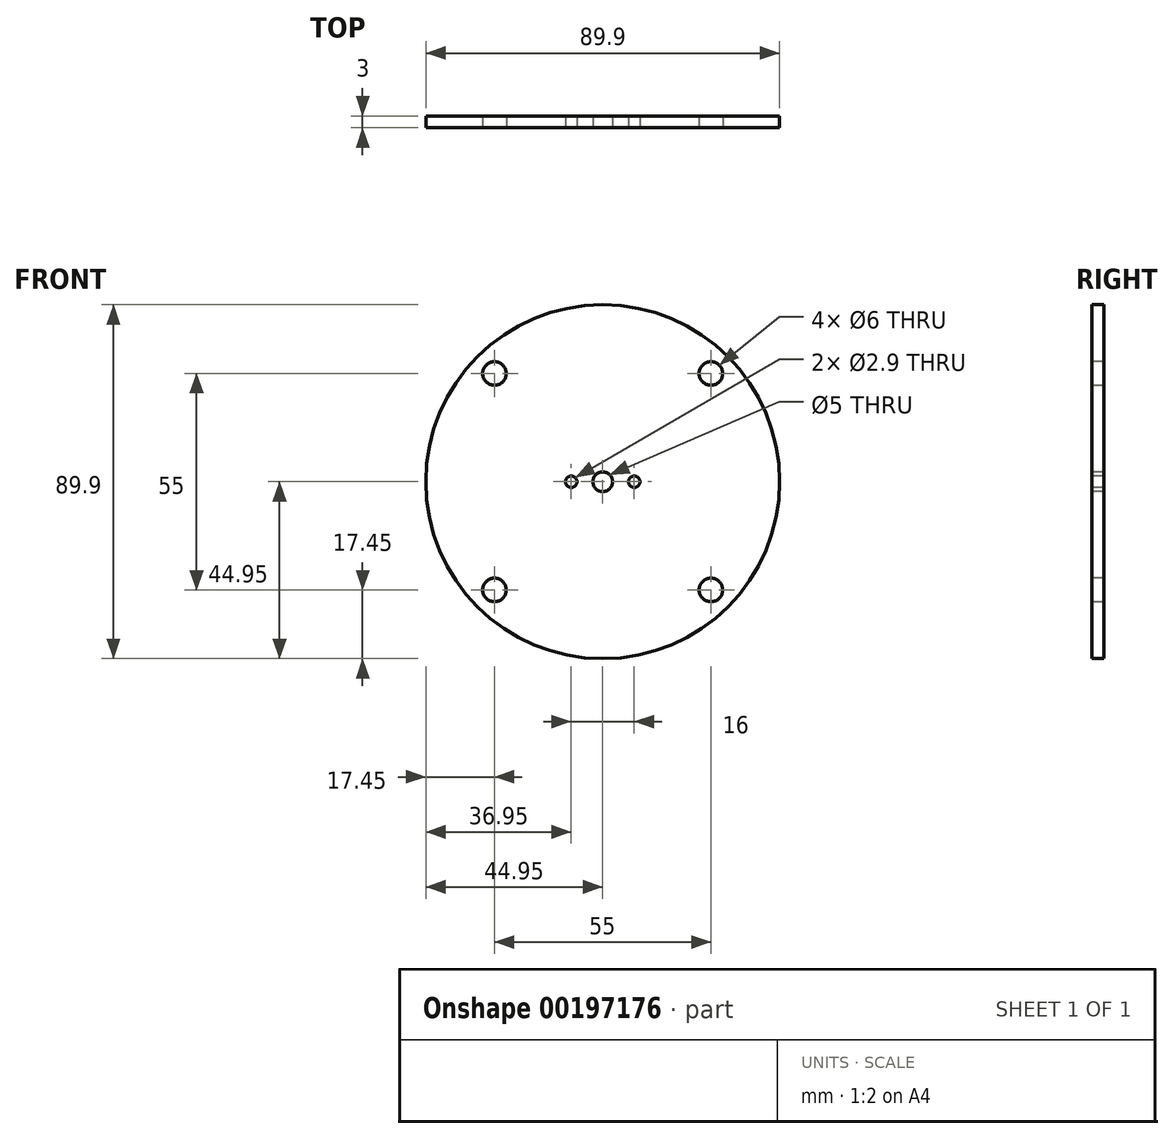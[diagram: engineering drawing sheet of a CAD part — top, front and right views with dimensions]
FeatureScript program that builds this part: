
annotation { "Feature Type Name" : "Feature", "Feature Type Description" : "" }
export const myFeature = defineFeature(function(context is Context, id is Id, definition is map)
    precondition{}
    {
        {
            var Q0;
            Q0=qCreatedBy(makeId("Front.planeOp"),FACE);
            var sketch = newSketch(context, id + "F0", { "sketchPlane" : qUnion([Q0])});
            skCircle(sketch, "E0", {"center": v(0, 0) * mm, "radius": 44.95 * mm});
            skSolve(sketch);
        }
        {
            var Q0;
            Q0=qSketchRegion(id+"F0",true);
            extrude(context, id + "F1", {"entities" : qUnion([Q0]), "depth" : 3 * mm});
        }
        {
            var Q0;
            Q0=makeQuery(id+"F1.opExtrude","CAP_FACE",FACE,{"disambiguationData":[OSD([sQuery(id+"F0.wireOp",EDGE,"E0")])],"isStart":false});
            var sketch = newSketch(context, id + "F2", { "sketchPlane" : qUnion([Q0])});
            skLineSegment(sketch, "E1", {"start": v(-44.95, 0) * mm, "end": v(44.95, 0) * mm, "construction": true});
            skLineSegment(sketch, "E2", {"start": v(0, 0) * mm, "end": v(0, 33.83) * mm, "construction": true});
            skCircle(sketch, "E3", {"center": v(-8, 0) * mm, "radius": 1.45 * mm});
            skCircle(sketch, "E4.MirrorC", {"center": v(8, 0) * mm, "radius": 1.45 * mm});
            skCircle(sketch, "E5", {"center": v(0, 0) * mm, "radius": 2.5 * mm});
            skSolve(sketch);
        }
        {
            var Q0;
            Q0=qSketchRegion(id+"F2",true);
            extrude(context, id + "F3", {"entities" : qUnion([Q0]), "operationType" : NewBodyOperationType.REMOVE, "endBound" : BoundingType.THROUGH_ALL, "oppositeDirection" : true, "depth" : 25 * mm});
        }
        {
            var Q0;
            Q0=makeQuery(id+"F1.opExtrude","CAP_FACE",FACE,{"disambiguationData":[OSD([sQuery(id+"F0.wireOp",EDGE,"E0")])],"isStart":false});
            var sketch = newSketch(context, id + "F4", { "sketchPlane" : qUnion([Q0])});
            skLineSegment(sketch, "E6", {"start": v(0, 0) * mm, "end": v(0, 23.9) * mm, "construction": true});
            skLineSegment(sketch, "E7", {"start": v(0, 0) * mm, "end": v(-31.3, 0) * mm, "construction": true});
            skCircle(sketch, "E8", {"center": v(-27.5, 27.5) * mm, "radius": 3 * mm});
            skCircle(sketch, "E9.MirrorC", {"center": v(27.5, 27.5) * mm, "radius": 3 * mm});
            skCircle(sketch, "E10.MirrorC", {"center": v(-27.5, -27.5) * mm, "radius": 3 * mm});
            skCircle(sketch, "E11.MirrorC", {"center": v(27.5, -27.5) * mm, "radius": 3 * mm});
            skSolve(sketch);
        }
        {
            var Q0;
            Q0=qSketchRegion(id+"F4",true);
            extrude(context, id + "F5", {"entities" : qUnion([Q0]), "operationType" : NewBodyOperationType.REMOVE, "endBound" : BoundingType.THROUGH_ALL, "oppositeDirection" : true, "depth" : 25 * mm});
        }
    });
